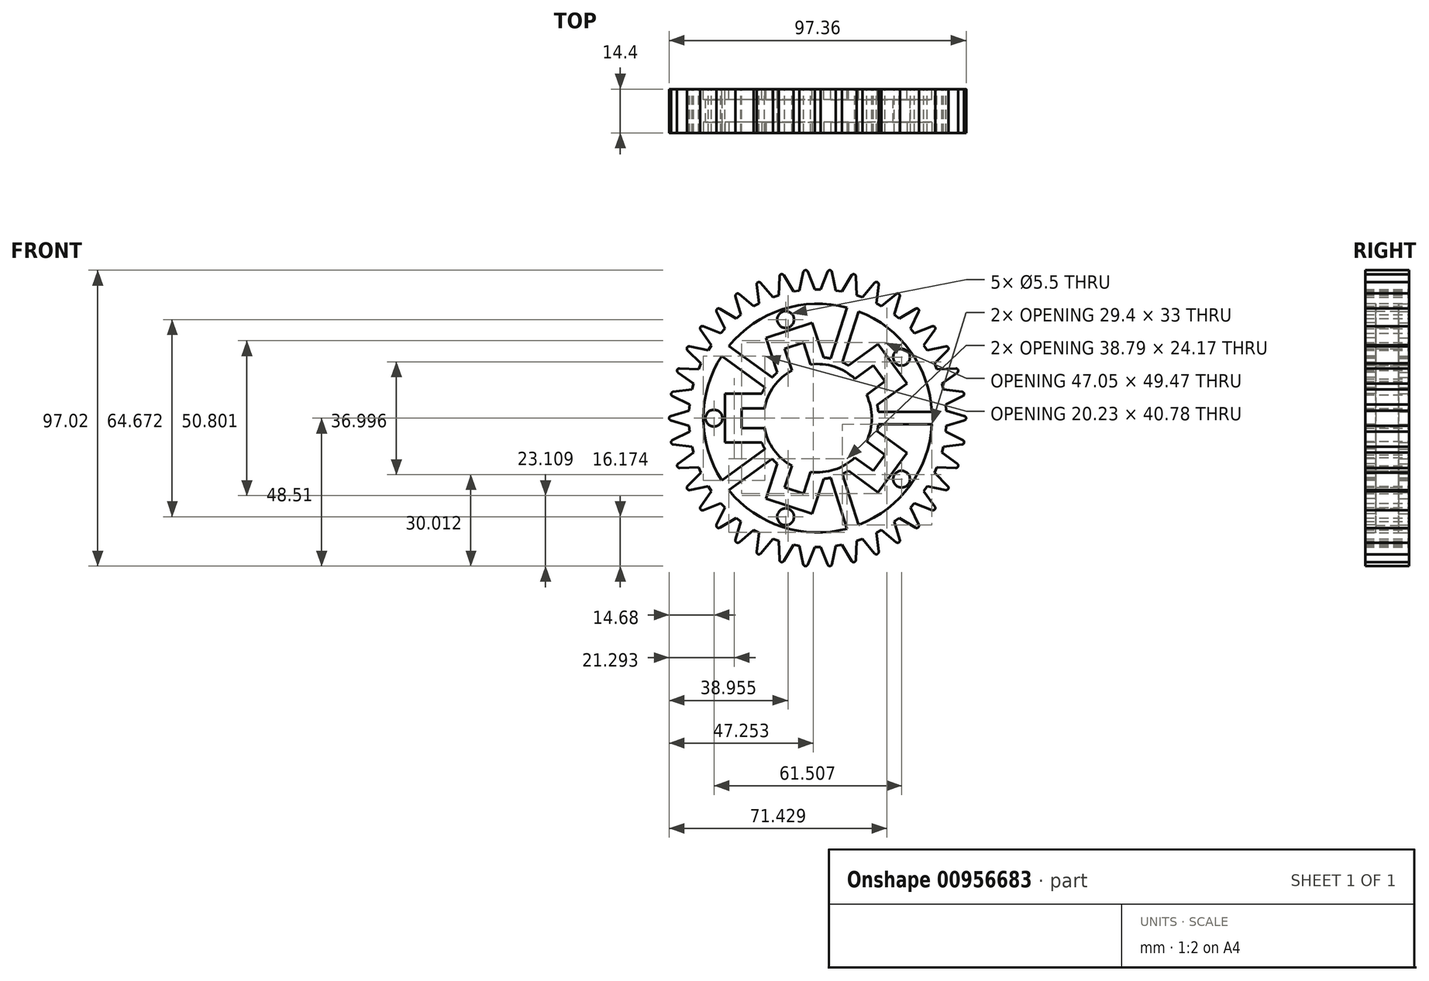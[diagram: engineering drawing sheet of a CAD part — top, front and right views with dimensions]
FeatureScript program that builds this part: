
annotation { "Feature Type Name" : "Feature", "Feature Type Description" : "" }
export const myFeature = defineFeature(function(context is Context, id is Id, definition is map)
    precondition{}
    {
        {
            var Q0;
            Q0=qCreatedBy(makeId("Front.planeOp"),FACE);
            var sketch = newSketch(context, id + "F0", { "sketchPlane" : qUnion([Q0])});
            skCircle(sketch, "E0", {"center": v(0, 0) * mm, "radius": 42.25 * mm, "construction": true});
            skCircle(sketch, "E1", {"center": v(0, 0) * mm, "radius": 17.75 * mm});
            skLineSegment(sketch, "E2", {"start": v(-54.02, 0) * mm, "end": v(59.41, 0) * mm, "construction": true});
            skLineSegment(sketch, "E3", {"start": v(-17.45, -3.25) * mm, "end": v(-24.95, -3.25) * mm});
            skLineSegment(sketch, "E4", {"start": v(-24.95, -3.25) * mm, "end": v(-24.95, 3.25) * mm});
            skLineSegment(sketch, "E5", {"start": v(-24.95, 3.25) * mm, "end": v(-17.45, 3.25) * mm});
            skPoint(sketch, "E6", {"position": v(-24.95, 0) * mm});
            skLineSegment(sketch, "E7.1.0", {"start": v(-10.8, -22.72) * mm, "end": v(-8.48, -15.6) * mm});
            skLineSegment(sketch, "E7.1.1", {"start": v(-4.62, -24.73) * mm, "end": v(-10.8, -22.72) * mm});
            skLineSegment(sketch, "E7.1.2", {"start": v(-2.3, -17.6) * mm, "end": v(-4.62, -24.73) * mm});
            skLineSegment(sketch, "E7.2.0", {"start": v(18.27, -17.3) * mm, "end": v(12.2, -12.89) * mm});
            skLineSegment(sketch, "E7.2.1", {"start": v(22.1, -12.04) * mm, "end": v(18.27, -17.3) * mm});
            skLineSegment(sketch, "E7.2.2", {"start": v(16.03, -7.63) * mm, "end": v(22.1, -12.04) * mm});
            skLineSegment(sketch, "E7.3.0", {"start": v(22.1, 12.04) * mm, "end": v(16.03, 7.63) * mm});
            skLineSegment(sketch, "E7.3.1", {"start": v(18.27, 17.3) * mm, "end": v(22.1, 12.04) * mm});
            skLineSegment(sketch, "E7.3.2", {"start": v(12.2, 12.89) * mm, "end": v(18.27, 17.3) * mm});
            skLineSegment(sketch, "E7.4.0", {"start": v(-4.62, 24.73) * mm, "end": v(-2.3, 17.6) * mm});
            skLineSegment(sketch, "E7.4.1", {"start": v(-10.8, 22.72) * mm, "end": v(-4.62, 24.73) * mm});
            skLineSegment(sketch, "E7.4.2", {"start": v(-8.48, 15.6) * mm, "end": v(-10.8, 22.72) * mm});
            skCircle(sketch, "E8", {"center": v(-34, 0) * mm, "radius": 2.75 * mm});
            skCircle(sketch, "E9.1.0", {"center": v(-10.5, -32.34) * mm, "radius": 2.75 * mm});
            skCircle(sketch, "E9.2.0", {"center": v(27.5, -19.98) * mm, "radius": 2.75 * mm});
            skCircle(sketch, "E9.3.0", {"center": v(27.5, 19.98) * mm, "radius": 2.75 * mm});
            skCircle(sketch, "E9.4.0", {"center": v(-10.5, 32.34) * mm, "radius": 2.75 * mm});
            skLineSegment(sketch, "E10", {"start": v(-42.18, 2.5) * mm, "end": v(-42.18, -2.5) * mm, "construction": true});
            skPoint(sketch, "E11", {"position": v(-42.18, 0) * mm});
            skLineSegment(sketch, "E12", {"start": v(-47.93, 0) * mm, "end": v(-42.18, 0) * mm, "construction": true});
            skArc(sketch, "E13", {"start": v(-48.14, 0.72) * mm, "mid": v(-48.68, 0) * mm, "end": v(-48.14, -0.72) * mm});
            skLineSegment(sketch, "E14", {"start": v(-42.18, -2.5) * mm, "end": v(-48.14, -0.72) * mm});
            skLineSegment(sketch, "E15", {"start": v(-42.18, 2.5) * mm, "end": v(-48.14, 0.72) * mm});
            skLineSegment(sketch, "E16.1.0", {"start": v(-41.19, -9.4) * mm, "end": v(-47.37, -8.63) * mm});
            skLineSegment(sketch, "E16.1.1", {"start": v(-42.01, -4.48) * mm, "end": v(-47.6, -7.21) * mm});
            skArc(sketch, "E16.1.2", {"start": v(-47.6, -7.21) * mm, "mid": v(-48.01, -8.01) * mm, "end": v(-47.37, -8.63) * mm});
            skLineSegment(sketch, "E16.2.0", {"start": v(-39.08, -16.06) * mm, "end": v(-45.3, -16.31) * mm});
            skLineSegment(sketch, "E16.2.1", {"start": v(-40.7, -11.33) * mm, "end": v(-45.77, -14.95) * mm});
            skArc(sketch, "E16.2.2", {"start": v(-45.77, -14.95) * mm, "mid": v(-46.04, -15.8) * mm, "end": v(-45.3, -16.31) * mm});
            skLineSegment(sketch, "E16.3.0", {"start": v(-35.9, -22.27) * mm, "end": v(-42, -23.54) * mm});
            skLineSegment(sketch, "E16.3.1", {"start": v(-38.28, -17.87) * mm, "end": v(-42.68, -22.28) * mm});
            skArc(sketch, "E16.3.2", {"start": v(-42.68, -22.28) * mm, "mid": v(-42.8, -23.17) * mm, "end": v(-42, -23.54) * mm});
            skLineSegment(sketch, "E16.4.0", {"start": v(-31.75, -27.88) * mm, "end": v(-37.55, -30.14) * mm});
            skLineSegment(sketch, "E16.4.1", {"start": v(-34.82, -23.93) * mm, "end": v(-38.43, -29) * mm});
            skArc(sketch, "E16.4.2", {"start": v(-38.43, -29) * mm, "mid": v(-38.41, -29.9) * mm, "end": v(-37.55, -30.14) * mm});
            skLineSegment(sketch, "E16.5.0", {"start": v(-26.73, -32.72) * mm, "end": v(-32.08, -35.9) * mm});
            skLineSegment(sketch, "E16.5.1", {"start": v(-30.4, -29.34) * mm, "end": v(-33.13, -34.93) * mm});
            skArc(sketch, "E16.5.2", {"start": v(-33.13, -34.93) * mm, "mid": v(-32.97, -35.81) * mm, "end": v(-32.08, -35.9) * mm});
            skLineSegment(sketch, "E16.6.0", {"start": v(-20.98, -36.68) * mm, "end": v(-25.73, -40.7) * mm});
            skLineSegment(sketch, "E16.6.1", {"start": v(-25.16, -33.94) * mm, "end": v(-26.93, -39.9) * mm});
            skArc(sketch, "E16.6.2", {"start": v(-26.93, -39.9) * mm, "mid": v(-26.62, -40.75) * mm, "end": v(-25.73, -40.7) * mm});
            skLineSegment(sketch, "E16.7.0", {"start": v(-14.65, -39.63) * mm, "end": v(-18.68, -44.37) * mm});
            skLineSegment(sketch, "E16.7.1", {"start": v(-19.23, -37.62) * mm, "end": v(-20, -43.8) * mm});
            skArc(sketch, "E16.7.2", {"start": v(-20, -43.8) * mm, "mid": v(-19.55, -44.58) * mm, "end": v(-18.68, -44.37) * mm});
            skLineSegment(sketch, "E16.8.0", {"start": v(-7.93, -41.5) * mm, "end": v(-11.12, -46.84) * mm});
            skLineSegment(sketch, "E16.8.1", {"start": v(-12.78, -40.27) * mm, "end": v(-12.51, -46.5) * mm});
            skArc(sketch, "E16.8.2", {"start": v(-12.51, -46.5) * mm, "mid": v(-11.95, -47.19) * mm, "end": v(-11.12, -46.84) * mm});
            skLineSegment(sketch, "E16.9.0", {"start": v(-1, -42.24) * mm, "end": v(-3.26, -48.04) * mm});
            skLineSegment(sketch, "E16.9.1", {"start": v(-5.97, -41.83) * mm, "end": v(-4.7, -47.92) * mm});
            skArc(sketch, "E16.9.2", {"start": v(-4.7, -47.92) * mm, "mid": v(-4.02, -48.5) * mm, "end": v(-3.26, -48.04) * mm});
            skLineSegment(sketch, "E16.10.0", {"start": v(5.97, -41.83) * mm, "end": v(4.7, -47.92) * mm});
            skLineSegment(sketch, "E16.10.1", {"start": v(1, -42.24) * mm, "end": v(3.26, -48.04) * mm});
            skArc(sketch, "E16.10.2", {"start": v(3.26, -48.04) * mm, "mid": v(4.02, -48.5) * mm, "end": v(4.7, -47.92) * mm});
            skLineSegment(sketch, "E16.11.0", {"start": v(12.78, -40.27) * mm, "end": v(12.51, -46.5) * mm});
            skLineSegment(sketch, "E16.11.1", {"start": v(7.93, -41.5) * mm, "end": v(11.12, -46.84) * mm});
            skArc(sketch, "E16.11.2", {"start": v(11.12, -46.84) * mm, "mid": v(11.95, -47.19) * mm, "end": v(12.51, -46.5) * mm});
            skLineSegment(sketch, "E16.12.0", {"start": v(19.23, -37.62) * mm, "end": v(20, -43.8) * mm});
            skLineSegment(sketch, "E16.12.1", {"start": v(14.65, -39.63) * mm, "end": v(18.68, -44.37) * mm});
            skArc(sketch, "E16.12.2", {"start": v(18.68, -44.37) * mm, "mid": v(19.55, -44.58) * mm, "end": v(20, -43.8) * mm});
            skLineSegment(sketch, "E16.13.0", {"start": v(25.16, -33.94) * mm, "end": v(26.93, -39.9) * mm});
            skLineSegment(sketch, "E16.13.1", {"start": v(20.98, -36.68) * mm, "end": v(25.73, -40.7) * mm});
            skArc(sketch, "E16.13.2", {"start": v(25.73, -40.7) * mm, "mid": v(26.62, -40.75) * mm, "end": v(26.93, -39.9) * mm});
            skLineSegment(sketch, "E16.14.0", {"start": v(30.4, -29.34) * mm, "end": v(33.13, -34.93) * mm});
            skLineSegment(sketch, "E16.14.1", {"start": v(26.73, -32.72) * mm, "end": v(32.08, -35.9) * mm});
            skArc(sketch, "E16.14.2", {"start": v(32.08, -35.9) * mm, "mid": v(32.97, -35.81) * mm, "end": v(33.13, -34.93) * mm});
            skLineSegment(sketch, "E16.15.0", {"start": v(34.82, -23.93) * mm, "end": v(38.43, -29) * mm});
            skLineSegment(sketch, "E16.15.1", {"start": v(31.75, -27.88) * mm, "end": v(37.55, -30.14) * mm});
            skArc(sketch, "E16.15.2", {"start": v(37.55, -30.14) * mm, "mid": v(38.41, -29.9) * mm, "end": v(38.43, -29) * mm});
            skLineSegment(sketch, "E16.16.0", {"start": v(38.28, -17.87) * mm, "end": v(42.68, -22.28) * mm});
            skLineSegment(sketch, "E16.16.1", {"start": v(35.9, -22.27) * mm, "end": v(42, -23.54) * mm});
            skArc(sketch, "E16.16.2", {"start": v(42, -23.54) * mm, "mid": v(42.8, -23.17) * mm, "end": v(42.68, -22.28) * mm});
            skLineSegment(sketch, "E16.17.0", {"start": v(40.7, -11.33) * mm, "end": v(45.77, -14.95) * mm});
            skLineSegment(sketch, "E16.17.1", {"start": v(39.08, -16.06) * mm, "end": v(45.3, -16.31) * mm});
            skArc(sketch, "E16.17.2", {"start": v(45.3, -16.31) * mm, "mid": v(46.04, -15.8) * mm, "end": v(45.77, -14.95) * mm});
            skLineSegment(sketch, "E16.18.0", {"start": v(42.01, -4.48) * mm, "end": v(47.6, -7.21) * mm});
            skLineSegment(sketch, "E16.18.1", {"start": v(41.19, -9.4) * mm, "end": v(47.37, -8.63) * mm});
            skArc(sketch, "E16.18.2", {"start": v(47.37, -8.63) * mm, "mid": v(48.01, -8.01) * mm, "end": v(47.6, -7.21) * mm});
            skLineSegment(sketch, "E16.19.0", {"start": v(42.18, 2.5) * mm, "end": v(48.14, 0.72) * mm});
            skLineSegment(sketch, "E16.19.1", {"start": v(42.18, -2.5) * mm, "end": v(48.14, -0.72) * mm});
            skArc(sketch, "E16.19.2", {"start": v(48.14, -0.72) * mm, "mid": v(48.68, 0) * mm, "end": v(48.14, 0.72) * mm});
            skLineSegment(sketch, "E16.20.0", {"start": v(41.19, 9.4) * mm, "end": v(47.37, 8.63) * mm});
            skLineSegment(sketch, "E16.20.1", {"start": v(42.01, 4.48) * mm, "end": v(47.6, 7.21) * mm});
            skArc(sketch, "E16.20.2", {"start": v(47.6, 7.21) * mm, "mid": v(48.01, 8.01) * mm, "end": v(47.37, 8.63) * mm});
            skLineSegment(sketch, "E16.21.0", {"start": v(39.08, 16.06) * mm, "end": v(45.3, 16.31) * mm});
            skLineSegment(sketch, "E16.21.1", {"start": v(40.7, 11.33) * mm, "end": v(45.77, 14.95) * mm});
            skArc(sketch, "E16.21.2", {"start": v(45.77, 14.95) * mm, "mid": v(46.04, 15.8) * mm, "end": v(45.3, 16.31) * mm});
            skLineSegment(sketch, "E16.22.0", {"start": v(35.9, 22.27) * mm, "end": v(42, 23.54) * mm});
            skLineSegment(sketch, "E16.22.1", {"start": v(38.28, 17.87) * mm, "end": v(42.68, 22.28) * mm});
            skArc(sketch, "E16.22.2", {"start": v(42.68, 22.28) * mm, "mid": v(42.8, 23.17) * mm, "end": v(42, 23.54) * mm});
            skLineSegment(sketch, "E16.23.0", {"start": v(31.75, 27.88) * mm, "end": v(37.55, 30.14) * mm});
            skLineSegment(sketch, "E16.23.1", {"start": v(34.82, 23.93) * mm, "end": v(38.43, 29) * mm});
            skArc(sketch, "E16.23.2", {"start": v(38.43, 29) * mm, "mid": v(38.41, 29.9) * mm, "end": v(37.55, 30.14) * mm});
            skLineSegment(sketch, "E16.24.0", {"start": v(26.73, 32.72) * mm, "end": v(32.08, 35.9) * mm});
            skLineSegment(sketch, "E16.24.1", {"start": v(30.4, 29.34) * mm, "end": v(33.13, 34.93) * mm});
            skArc(sketch, "E16.24.2", {"start": v(33.13, 34.93) * mm, "mid": v(32.97, 35.81) * mm, "end": v(32.08, 35.9) * mm});
            skLineSegment(sketch, "E16.25.0", {"start": v(20.98, 36.68) * mm, "end": v(25.73, 40.7) * mm});
            skLineSegment(sketch, "E16.25.1", {"start": v(25.16, 33.94) * mm, "end": v(26.93, 39.9) * mm});
            skArc(sketch, "E16.25.2", {"start": v(26.93, 39.9) * mm, "mid": v(26.62, 40.75) * mm, "end": v(25.73, 40.7) * mm});
            skLineSegment(sketch, "E16.26.0", {"start": v(14.65, 39.63) * mm, "end": v(18.68, 44.37) * mm});
            skLineSegment(sketch, "E16.26.1", {"start": v(19.23, 37.62) * mm, "end": v(20, 43.8) * mm});
            skArc(sketch, "E16.26.2", {"start": v(20, 43.8) * mm, "mid": v(19.55, 44.58) * mm, "end": v(18.68, 44.37) * mm});
            skLineSegment(sketch, "E16.27.0", {"start": v(7.93, 41.5) * mm, "end": v(11.12, 46.84) * mm});
            skLineSegment(sketch, "E16.27.1", {"start": v(12.78, 40.27) * mm, "end": v(12.51, 46.5) * mm});
            skArc(sketch, "E16.27.2", {"start": v(12.51, 46.5) * mm, "mid": v(11.95, 47.19) * mm, "end": v(11.12, 46.84) * mm});
            skLineSegment(sketch, "E16.28.0", {"start": v(1, 42.24) * mm, "end": v(3.26, 48.04) * mm});
            skLineSegment(sketch, "E16.28.1", {"start": v(5.97, 41.83) * mm, "end": v(4.7, 47.92) * mm});
            skArc(sketch, "E16.28.2", {"start": v(4.7, 47.92) * mm, "mid": v(4.02, 48.5) * mm, "end": v(3.26, 48.04) * mm});
            skLineSegment(sketch, "E16.29.0", {"start": v(-5.97, 41.83) * mm, "end": v(-4.7, 47.92) * mm});
            skLineSegment(sketch, "E16.29.1", {"start": v(-1, 42.24) * mm, "end": v(-3.26, 48.04) * mm});
            skArc(sketch, "E16.29.2", {"start": v(-3.26, 48.04) * mm, "mid": v(-4.02, 48.5) * mm, "end": v(-4.7, 47.92) * mm});
            skLineSegment(sketch, "E16.30.0", {"start": v(-12.78, 40.27) * mm, "end": v(-12.51, 46.5) * mm});
            skLineSegment(sketch, "E16.30.1", {"start": v(-7.93, 41.5) * mm, "end": v(-11.12, 46.84) * mm});
            skArc(sketch, "E16.30.2", {"start": v(-11.12, 46.84) * mm, "mid": v(-11.95, 47.19) * mm, "end": v(-12.51, 46.5) * mm});
            skLineSegment(sketch, "E16.31.0", {"start": v(-19.23, 37.62) * mm, "end": v(-20, 43.8) * mm});
            skLineSegment(sketch, "E16.31.1", {"start": v(-14.65, 39.63) * mm, "end": v(-18.68, 44.37) * mm});
            skArc(sketch, "E16.31.2", {"start": v(-18.68, 44.37) * mm, "mid": v(-19.55, 44.58) * mm, "end": v(-20, 43.8) * mm});
            skLineSegment(sketch, "E16.32.0", {"start": v(-25.16, 33.94) * mm, "end": v(-26.93, 39.9) * mm});
            skLineSegment(sketch, "E16.32.1", {"start": v(-20.98, 36.68) * mm, "end": v(-25.73, 40.7) * mm});
            skArc(sketch, "E16.32.2", {"start": v(-25.73, 40.7) * mm, "mid": v(-26.62, 40.75) * mm, "end": v(-26.93, 39.9) * mm});
            skLineSegment(sketch, "E16.33.0", {"start": v(-30.4, 29.34) * mm, "end": v(-33.13, 34.93) * mm});
            skLineSegment(sketch, "E16.33.1", {"start": v(-26.73, 32.72) * mm, "end": v(-32.08, 35.9) * mm});
            skArc(sketch, "E16.33.2", {"start": v(-32.08, 35.9) * mm, "mid": v(-32.97, 35.81) * mm, "end": v(-33.13, 34.93) * mm});
            skLineSegment(sketch, "E16.34.0", {"start": v(-34.82, 23.93) * mm, "end": v(-38.43, 29) * mm});
            skLineSegment(sketch, "E16.34.1", {"start": v(-31.75, 27.88) * mm, "end": v(-37.55, 30.14) * mm});
            skArc(sketch, "E16.34.2", {"start": v(-37.55, 30.14) * mm, "mid": v(-38.41, 29.9) * mm, "end": v(-38.43, 29) * mm});
            skLineSegment(sketch, "E16.35.0", {"start": v(-38.28, 17.87) * mm, "end": v(-42.68, 22.28) * mm});
            skLineSegment(sketch, "E16.35.1", {"start": v(-35.9, 22.27) * mm, "end": v(-42, 23.54) * mm});
            skArc(sketch, "E16.35.2", {"start": v(-42, 23.54) * mm, "mid": v(-42.8, 23.17) * mm, "end": v(-42.68, 22.28) * mm});
            skLineSegment(sketch, "E16.36.0", {"start": v(-40.7, 11.33) * mm, "end": v(-45.77, 14.95) * mm});
            skLineSegment(sketch, "E16.36.1", {"start": v(-39.08, 16.06) * mm, "end": v(-45.3, 16.31) * mm});
            skArc(sketch, "E16.36.2", {"start": v(-45.3, 16.31) * mm, "mid": v(-46.04, 15.8) * mm, "end": v(-45.77, 14.95) * mm});
            skLineSegment(sketch, "E16.37.0", {"start": v(-42.01, 4.48) * mm, "end": v(-47.6, 7.21) * mm});
            skLineSegment(sketch, "E16.37.1", {"start": v(-41.19, 9.4) * mm, "end": v(-47.37, 8.63) * mm});
            skArc(sketch, "E16.37.2", {"start": v(-47.37, 8.63) * mm, "mid": v(-48.01, 8.01) * mm, "end": v(-47.6, 7.21) * mm});
            skLineSegment(sketch, "E17", {"start": v(-42.18, 2.5) * mm, "end": v(-42.01, 4.48) * mm});
            skLineSegment(sketch, "E18.1.0", {"start": v(-42.01, -4.48) * mm, "end": v(-42.18, -2.5) * mm});
            skLineSegment(sketch, "E18.2.0", {"start": v(-40.7, -11.33) * mm, "end": v(-41.19, -9.4) * mm});
            skLineSegment(sketch, "E18.3.0", {"start": v(-38.28, -17.87) * mm, "end": v(-39.08, -16.06) * mm});
            skLineSegment(sketch, "E18.4.0", {"start": v(-34.82, -23.93) * mm, "end": v(-35.9, -22.27) * mm});
            skLineSegment(sketch, "E18.5.0", {"start": v(-30.4, -29.34) * mm, "end": v(-31.75, -27.88) * mm});
            skLineSegment(sketch, "E18.6.0", {"start": v(-25.16, -33.94) * mm, "end": v(-26.73, -32.72) * mm});
            skLineSegment(sketch, "E18.7.0", {"start": v(-19.23, -37.62) * mm, "end": v(-20.98, -36.68) * mm});
            skLineSegment(sketch, "E18.8.0", {"start": v(-12.78, -40.27) * mm, "end": v(-14.65, -39.63) * mm});
            skLineSegment(sketch, "E18.9.0", {"start": v(-5.97, -41.83) * mm, "end": v(-7.93, -41.5) * mm});
            skLineSegment(sketch, "E18.10.0", {"start": v(1, -42.24) * mm, "end": v(-1, -42.24) * mm});
            skLineSegment(sketch, "E18.11.0", {"start": v(7.93, -41.5) * mm, "end": v(5.97, -41.83) * mm});
            skLineSegment(sketch, "E18.12.0", {"start": v(14.65, -39.63) * mm, "end": v(12.78, -40.27) * mm});
            skLineSegment(sketch, "E18.13.0", {"start": v(20.98, -36.68) * mm, "end": v(19.23, -37.62) * mm});
            skLineSegment(sketch, "E18.14.0", {"start": v(26.73, -32.72) * mm, "end": v(25.16, -33.94) * mm});
            skLineSegment(sketch, "E18.15.0", {"start": v(31.75, -27.88) * mm, "end": v(30.4, -29.34) * mm});
            skLineSegment(sketch, "E18.16.0", {"start": v(35.9, -22.27) * mm, "end": v(34.82, -23.93) * mm});
            skLineSegment(sketch, "E18.17.0", {"start": v(39.08, -16.06) * mm, "end": v(38.28, -17.87) * mm});
            skLineSegment(sketch, "E18.18.0", {"start": v(41.19, -9.4) * mm, "end": v(40.7, -11.33) * mm});
            skLineSegment(sketch, "E18.19.0", {"start": v(42.18, -2.5) * mm, "end": v(42.01, -4.48) * mm});
            skLineSegment(sketch, "E18.20.0", {"start": v(42.01, 4.48) * mm, "end": v(42.18, 2.5) * mm});
            skLineSegment(sketch, "E18.21.0", {"start": v(40.7, 11.33) * mm, "end": v(41.19, 9.4) * mm});
            skLineSegment(sketch, "E18.22.0", {"start": v(38.28, 17.87) * mm, "end": v(39.08, 16.06) * mm});
            skLineSegment(sketch, "E18.23.0", {"start": v(34.82, 23.93) * mm, "end": v(35.9, 22.27) * mm});
            skLineSegment(sketch, "E18.24.0", {"start": v(30.4, 29.34) * mm, "end": v(31.75, 27.88) * mm});
            skLineSegment(sketch, "E18.25.0", {"start": v(25.16, 33.94) * mm, "end": v(26.73, 32.72) * mm});
            skLineSegment(sketch, "E18.26.0", {"start": v(19.23, 37.62) * mm, "end": v(20.98, 36.68) * mm});
            skLineSegment(sketch, "E18.27.0", {"start": v(12.78, 40.27) * mm, "end": v(14.65, 39.63) * mm});
            skLineSegment(sketch, "E18.28.0", {"start": v(5.97, 41.83) * mm, "end": v(7.93, 41.5) * mm});
            skLineSegment(sketch, "E18.29.0", {"start": v(-1, 42.24) * mm, "end": v(1, 42.24) * mm});
            skLineSegment(sketch, "E18.30.0", {"start": v(-7.93, 41.5) * mm, "end": v(-5.97, 41.83) * mm});
            skLineSegment(sketch, "E18.31.0", {"start": v(-14.65, 39.63) * mm, "end": v(-12.78, 40.27) * mm});
            skLineSegment(sketch, "E18.32.0", {"start": v(-20.98, 36.68) * mm, "end": v(-19.23, 37.62) * mm});
            skLineSegment(sketch, "E18.33.0", {"start": v(-26.73, 32.72) * mm, "end": v(-25.16, 33.94) * mm});
            skLineSegment(sketch, "E18.34.0", {"start": v(-31.75, 27.88) * mm, "end": v(-30.4, 29.34) * mm});
            skLineSegment(sketch, "E18.35.0", {"start": v(-35.9, 22.27) * mm, "end": v(-34.82, 23.93) * mm});
            skLineSegment(sketch, "E18.36.0", {"start": v(-39.08, 16.06) * mm, "end": v(-38.28, 17.87) * mm});
            skLineSegment(sketch, "E18.37.0", {"start": v(-41.19, 9.4) * mm, "end": v(-40.7, 11.33) * mm});
            skSolve(sketch);
        }
        {
            var Q0;
            {var subQ4=sQuery(id+"F0.wireOp",EDGE,"E3");Q0=makeQuery(id+"F0.imprint","IMPRINT",FACE,{"disambiguationData":[TD([[makeQuery(id+"F0.imprint","IMPRINT",EDGE,{"derivedFrom":subQ4}),1.0]])]});}
            extrude(context, id + "F1", {"entities" : qUnion([Q0]), "depth" : 7.2 * mm, "offsetDistance" : 25 * mm});
        }
        {
            var Q0;
            Q0=makeQuery(id+"F1.opExtrude","CAP_FACE",FACE,{"disambiguationData":[OSD([sQuery(id+"F0.wireOp",EDGE,"E0"),sQuery(id+"F0.wireOp",EDGE,"E1"),sQuery(id+"F0.wireOp",EDGE,"E3"),sQuery(id+"F0.wireOp",EDGE,"E4"),sQuery(id+"F0.wireOp",EDGE,"E5"),sQuery(id+"F0.wireOp",EDGE,"E7.1.0"),sQuery(id+"F0.wireOp",EDGE,"E7.1.1"),sQuery(id+"F0.wireOp",EDGE,"E7.1.2"),sQuery(id+"F0.wireOp",EDGE,"E7.2.0"),sQuery(id+"F0.wireOp",EDGE,"E7.2.1"),sQuery(id+"F0.wireOp",EDGE,"E7.2.2"),sQuery(id+"F0.wireOp",EDGE,"E7.3.0"),sQuery(id+"F0.wireOp",EDGE,"E7.3.1"),sQuery(id+"F0.wireOp",EDGE,"E7.3.2"),sQuery(id+"F0.wireOp",EDGE,"E7.4.0"),sQuery(id+"F0.wireOp",EDGE,"E7.4.1"),sQuery(id+"F0.wireOp",EDGE,"E7.4.2"),sQuery(id+"F0.wireOp",EDGE,"E8"),sQuery(id+"F0.wireOp",EDGE,"E9.1.0"),sQuery(id+"F0.wireOp",EDGE,"E9.2.0"),sQuery(id+"F0.wireOp",EDGE,"E9.3.0"),sQuery(id+"F0.wireOp",EDGE,"E9.4.0")])],"isStart":false});
            var sketch = newSketch(context, id + "F2", { "sketchPlane" : qUnion([Q0])});
            skCircle(sketch, "E19", {"center": v(0, 0) * mm, "radius": 20 * mm});
            skLineSegment(sketch, "E20", {"start": v(-52.8, 0) * mm, "end": v(60.64, 0) * mm, "construction": true});
            skLineSegment(sketch, "E21", {"start": v(-18.33, -8) * mm, "end": v(-30.33, -8) * mm});
            skLineSegment(sketch, "E22", {"start": v(-30.33, -8) * mm, "end": v(-30.33, 8) * mm});
            skLineSegment(sketch, "E23", {"start": v(-30.33, 8) * mm, "end": v(-18.33, 8) * mm});
            skPoint(sketch, "E24", {"position": v(-30.33, 0) * mm});
            skLineSegment(sketch, "E25.1.0", {"start": v(-16.98, -26.37) * mm, "end": v(-13.27, -14.96) * mm});
            skLineSegment(sketch, "E25.1.1", {"start": v(-1.76, -31.32) * mm, "end": v(-16.98, -26.37) * mm});
            skLineSegment(sketch, "E25.1.2", {"start": v(1.94, -19.9) * mm, "end": v(-1.76, -31.32) * mm});
            skLineSegment(sketch, "E25.2.0", {"start": v(19.84, -24.3) * mm, "end": v(10.13, -17.25) * mm});
            skLineSegment(sketch, "E25.2.1", {"start": v(29.24, -11.36) * mm, "end": v(19.84, -24.3) * mm});
            skLineSegment(sketch, "E25.2.2", {"start": v(19.53, -4.3) * mm, "end": v(29.24, -11.36) * mm});
            skLineSegment(sketch, "E25.3.0", {"start": v(29.24, 11.36) * mm, "end": v(19.53, 4.3) * mm});
            skLineSegment(sketch, "E25.3.1", {"start": v(19.84, 24.3) * mm, "end": v(29.24, 11.36) * mm});
            skLineSegment(sketch, "E25.3.2", {"start": v(10.13, 17.25) * mm, "end": v(19.84, 24.3) * mm});
            skLineSegment(sketch, "E25.4.0", {"start": v(-1.76, 31.32) * mm, "end": v(1.94, 19.9) * mm});
            skLineSegment(sketch, "E25.4.1", {"start": v(-16.98, 26.37) * mm, "end": v(-1.76, 31.32) * mm});
            skLineSegment(sketch, "E25.4.2", {"start": v(-13.27, 14.96) * mm, "end": v(-16.98, 26.37) * mm});
            skCircle(sketch, "E26", {"center": v(0, 0) * mm, "radius": 37.5 * mm});
            skCircle(sketch, "E27", {"center": v(0, 0) * mm, "radius": 17.75 * mm});
            skLineSegment(sketch, "E28", {"start": v(17.64, 2) * mm, "end": v(37.45, 2) * mm});
            skLineSegment(sketch, "E29", {"start": v(17.64, -2) * mm, "end": v(37.45, -2) * mm});
            skLineSegment(sketch, "E30.1.0", {"start": v(3.55, 17.4) * mm, "end": v(9.67, 36.23) * mm});
            skLineSegment(sketch, "E30.1.1", {"start": v(7.35, 16.16) * mm, "end": v(13.47, 35) * mm});
            skLineSegment(sketch, "E30.2.0", {"start": v(-15.44, 8.75) * mm, "end": v(-31.47, 20.4) * mm});
            skLineSegment(sketch, "E30.2.1", {"start": v(-13.1, 11.98) * mm, "end": v(-29.12, 23.63) * mm});
            skLineSegment(sketch, "E30.3.0", {"start": v(-13.1, -11.98) * mm, "end": v(-29.12, -23.63) * mm});
            skLineSegment(sketch, "E30.3.1", {"start": v(-15.44, -8.75) * mm, "end": v(-31.47, -20.4) * mm});
            skLineSegment(sketch, "E30.4.0", {"start": v(7.35, -16.16) * mm, "end": v(13.47, -35) * mm});
            skLineSegment(sketch, "E30.4.1", {"start": v(3.55, -17.4) * mm, "end": v(9.67, -36.23) * mm});
            skSolve(sketch);
        }
        {
            var Q0;
            {var subQ19=sQuery(id+"F2.wireOp",EDGE,"E22");Q0=makeQuery(id+"F2.imprint","IMPRINT",FACE,{"disambiguationData":[TD([[makeQuery(id+"F2.imprint","IMPRINT",EDGE,{"derivedFrom":subQ19}),1.0]])]});}
            var Q1;
            {var subQ1=sQuery(id+"F2.wireOp",EDGE,"E25.4.1");Q1=makeQuery(id+"F2.imprint","IMPRINT",FACE,{"disambiguationData":[TD([[makeQuery(id+"F2.imprint","IMPRINT",EDGE,{"derivedFrom":subQ1}),1.0]])]});}
            var Q2;
            {var subQ1=sQuery(id+"F2.wireOp",EDGE,"E25.3.1");Q2=makeQuery(id+"F2.imprint","IMPRINT",FACE,{"disambiguationData":[TD([[makeQuery(id+"F2.imprint","IMPRINT",EDGE,{"derivedFrom":subQ1}),1.0]])]});}
            var Q3;
            {var subQ4=sQuery(id+"F2.wireOp",EDGE,"E25.2.1");Q3=makeQuery(id+"F2.imprint","IMPRINT",FACE,{"disambiguationData":[TD([[makeQuery(id+"F2.imprint","IMPRINT",EDGE,{"derivedFrom":subQ4}),1.0]])]});}
            var Q4;
            {var subQ4=sQuery(id+"F2.wireOp",EDGE,"E25.1.1");Q4=makeQuery(id+"F2.imprint","IMPRINT",FACE,{"disambiguationData":[TD([[makeQuery(id+"F2.imprint","IMPRINT",EDGE,{"derivedFrom":subQ4}),1.0]])]});}
            extrude(context, id + "F3", {"entities" : qUnion([Q0, Q1, Q2, Q3, Q4]), "operationType" : NewBodyOperationType.REMOVE, "endBound" : BoundingType.SYMMETRIC, "oppositeDirection" : true, "depth" : 7 * mm, "offsetDistance" : 25 * mm});
        }
        {
            var Q0;
            Q0=makeQuery(id+"F1.opExtrude","SWEPT_BODY",BODY,{"disambiguationData":[OSD([sQuery(id+"F0.wireOp",EDGE,"E0"),sQuery(id+"F0.wireOp",EDGE,"E1"),sQuery(id+"F0.wireOp",EDGE,"E3"),sQuery(id+"F0.wireOp",EDGE,"E4"),sQuery(id+"F0.wireOp",EDGE,"E5"),sQuery(id+"F0.wireOp",EDGE,"E7.1.0"),sQuery(id+"F0.wireOp",EDGE,"E7.1.1"),sQuery(id+"F0.wireOp",EDGE,"E7.1.2"),sQuery(id+"F0.wireOp",EDGE,"E7.2.0"),sQuery(id+"F0.wireOp",EDGE,"E7.2.1"),sQuery(id+"F0.wireOp",EDGE,"E7.2.2"),sQuery(id+"F0.wireOp",EDGE,"E7.3.0"),sQuery(id+"F0.wireOp",EDGE,"E7.3.1"),sQuery(id+"F0.wireOp",EDGE,"E7.3.2"),sQuery(id+"F0.wireOp",EDGE,"E7.4.0"),sQuery(id+"F0.wireOp",EDGE,"E7.4.1"),sQuery(id+"F0.wireOp",EDGE,"E7.4.2"),sQuery(id+"F0.wireOp",EDGE,"E8"),sQuery(id+"F0.wireOp",EDGE,"E9.1.0"),sQuery(id+"F0.wireOp",EDGE,"E9.2.0"),sQuery(id+"F0.wireOp",EDGE,"E9.3.0"),sQuery(id+"F0.wireOp",EDGE,"E9.4.0")])]});
            var Q1;
            Q1=makeQuery(id+"F1.opExtrude","CAP_FACE",FACE,{"disambiguationData":[OSD([sQuery(id+"F0.wireOp",EDGE,"E0"),sQuery(id+"F0.wireOp",EDGE,"E1"),sQuery(id+"F0.wireOp",EDGE,"E3"),sQuery(id+"F0.wireOp",EDGE,"E4"),sQuery(id+"F0.wireOp",EDGE,"E5"),sQuery(id+"F0.wireOp",EDGE,"E7.1.0"),sQuery(id+"F0.wireOp",EDGE,"E7.1.1"),sQuery(id+"F0.wireOp",EDGE,"E7.1.2"),sQuery(id+"F0.wireOp",EDGE,"E7.2.0"),sQuery(id+"F0.wireOp",EDGE,"E7.2.1"),sQuery(id+"F0.wireOp",EDGE,"E7.2.2"),sQuery(id+"F0.wireOp",EDGE,"E7.3.0"),sQuery(id+"F0.wireOp",EDGE,"E7.3.1"),sQuery(id+"F0.wireOp",EDGE,"E7.3.2"),sQuery(id+"F0.wireOp",EDGE,"E7.4.0"),sQuery(id+"F0.wireOp",EDGE,"E7.4.1"),sQuery(id+"F0.wireOp",EDGE,"E7.4.2"),sQuery(id+"F0.wireOp",EDGE,"E8"),sQuery(id+"F0.wireOp",EDGE,"E9.1.0"),sQuery(id+"F0.wireOp",EDGE,"E9.2.0"),sQuery(id+"F0.wireOp",EDGE,"E9.3.0"),sQuery(id+"F0.wireOp",EDGE,"E9.4.0")])],"isStart":true});
            mirror(context, id + "F4", {"operationType" : NewBodyOperationType.ADD, "entities" : qUnion([Q0]), "mirrorPlane" : qUnion([Q1])});
        }
    });
